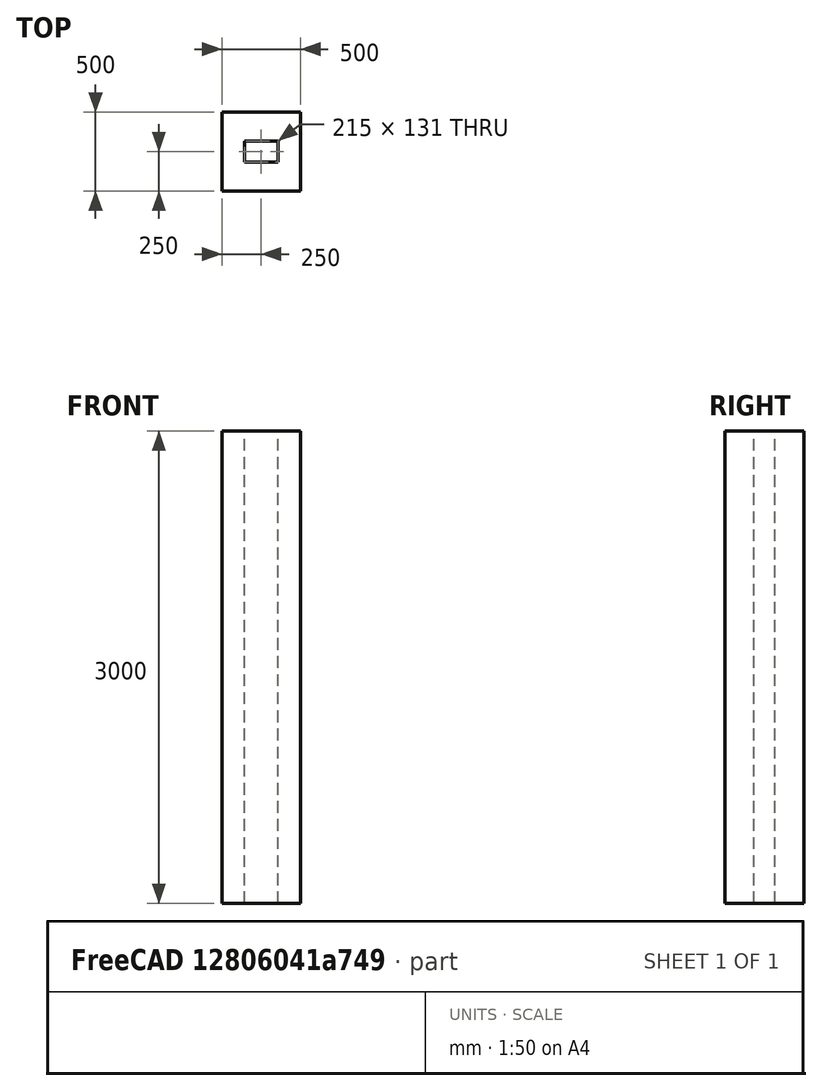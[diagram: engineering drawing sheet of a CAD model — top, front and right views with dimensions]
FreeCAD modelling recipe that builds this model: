
FCSTD DOCUMENT  (FreeCAD 0.21R33771 (Git))
Label: PQ4_yolk
License: All rights reserved
LicenseURL: https://en.wikipedia.org/wiki/All_rights_reserved
objects: Sketcher::SketchObject×1, PartDesign::Pad×1, PartDesign::Body×1
note: 4 computed .brp shape members not serialized (recipe doc carries the construction recipe); baked Part::Feature solids carry a one-line shape summary decoded from their .brp

FEATURE [Sketcher::SketchObject] Sketch
  FullyConstrained = true
  MapMode = 5
  Support = -> [XY_Plane]
  sketch-geometry (10):
    g0: LineSegment StartX=-250 StartY=-250 StartZ=0 EndX=-250 EndY=250 EndZ=0
    g1: LineSegment StartX=-250 StartY=250 StartZ=0 EndX=250 EndY=250 EndZ=0
    g2: LineSegment StartX=250 StartY=250 StartZ=0 EndX=250 EndY=-250 EndZ=0
    g3: LineSegment StartX=250 StartY=-250 StartZ=0 EndX=-250 EndY=-250 EndZ=0
    g4: GeomPoint X=0 Y=0 Z=0
    g5: LineSegment StartX=-107.5 StartY=-65.5 StartZ=0 EndX=-107.5 EndY=65.5 EndZ=0
    g6: LineSegment StartX=-107.5 StartY=65.5 StartZ=0 EndX=107.5 EndY=65.5 EndZ=0
    g7: LineSegment StartX=107.5 StartY=65.5 StartZ=0 EndX=107.5 EndY=-65.5 EndZ=0
    g8: LineSegment StartX=107.5 StartY=-65.5 StartZ=0 EndX=-107.5 EndY=-65.5 EndZ=0
    g9: GeomPoint X=0 Y=0 Z=0
  constraints (24):
    c: Coincident(g0,g1)
    c: Coincident(g1,g2)
    c: Coincident(g2,g3)
    c: Coincident(g3,g0)
    c: Horizontal(g1)
    c: Horizontal(g3)
    c: Vertical(g0)
    c: Vertical(g2)
    c: Symmetric(g1,g0,g4)
    c: Coincident(g4,g-1)
    c: DistanceX(g1,g1) = 500
    c: DistanceY(g2,g2) = 500
    c: Coincident(g5,g6)
    c: Coincident(g6,g7)
    c: Coincident(g7,g8)
    c: Coincident(g8,g5)
    c: Horizontal(g6)
    c: Horizontal(g8)
    c: Vertical(g5)
    c: Vertical(g7)
    c: Symmetric(g6,g5,g9)
    c: Coincident(g9,g4)
    c: DistanceX(g6,g6) = 215
    c: DistanceY(g7,g7) = 131
FEATURE [PartDesign::Pad] Pad
  Direction = (0,0,1)
  Length = 3000
  Length2 = 10
  Midplane = true
  Profile = -> Sketch
  ReferenceAxis = -> Sketch [N_Axis]
  Type = 0
FEATURE [PartDesign::Body] Body
  Group = -> [Sketch,Pad]
  Origin = -> Origin
  Tip = -> Pad
